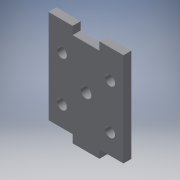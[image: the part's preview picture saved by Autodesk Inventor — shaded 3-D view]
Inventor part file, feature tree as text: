
AUTODESK INVENTOR PART (.ipt)
format: ipt  version: 2018 (Build 220112000, 112)  size: 145,408 bytes
history: native  units: in
note: dims shown in document units (in); Inventor stores cm internally (conversion verified against a paired STEP export)
features: reference x17, other x6, extrude x5, sketch x5
ambient origin geometry x8: Origin, YZ Plane, XZ Plane, XY Plane, X Axis, Y Axis, Z Axis, Center Point
bodies: Solid1 (feature_tree)
feature tree (33):
  extrude  "Extrusion1"  Depth=0.1181in TaperAngle=0.0deg
  extrude  "Extrusion2"  Depth=0.1575in
  extrude  "Extrusion3"  Depth=0.1181in TaperAngle=0.0deg
  extrude  "Extrusion4"  [1 undecoded]
  extrude  "Extrusion5"  [1 undecoded]
  sketch  "Sketch1"  dims[d0=1.378in d1=0.1181in d2=0.0in]
  reference  "Reference1"
  reference  "Reference2"
  reference  "Reference3"
  reference  "Reference4"
  sketch  "Sketch2"  dims[d3=0.2431in d4=0.0in d5=0.1575in]
  reference  "Reference5"
  reference  "Reference6"
  reference  "Reference7"
  reference  "Reference8"
  reference  "Reference9"
  reference  "Reference10"
  reference  "Reference11"
  reference  "Reference12"
  sketch  "Sketch3"  dims[d6=0.2431in d7=0.0in d8=0.1181in d9=0.0in]
  sketch  "Sketch4"  dims[d10=0.1181in d11=0.0in]
  reference  "Reference13"
  reference  "Reference14"
  reference  "Reference15"
  sketch  "Sketch5"
  reference  "Reference16"
  reference  "Reference17"
  other  "Camera pan and tilt assembly.iam"
  other  "Camera holder plate:1"
  other  "Angle bracket short:1"
  other  "Angle bracket short:2"
  other  "Angle bracket short:9"
  other  "Angle bracket short:10"
note: 2 required parameter values undecoded (feature->parameter linkage not recoverable at this tier; creation-order binding heuristic only, values carry confidence <= 0.55)
